# Revit family: Genie_Site_ScissorLift_GS4655a
name_source: partatom
category: Site
revit_build: Autodesk Revit 2018 (Build: 20190510_1515(x64)
units: mm (PartAtom-declared; Revit-internal decimal feet)

## family parameters
Always vertical = Yes
Cut with Voids When Loaded = No
OmniClass Number = 23.50.85.17.11
OmniClass Title = Electric and Battery Telescoping Platforms
Part Type = Normal
Round Connector Dimension = Use Diameter
Shared = No
Work Plane-Based = No

## types (1)
- GS4655
    Assembly Code = E1030900
    AssetType = Fixed
    BIMObjectName = Genie_Site_ScissorLift_GS4655
    BaseHeight = 595 mm  [stored 1.9521 ft]
    BasketHeight = 1210 mm
    C = 2640 mm
    ClassificationName = Uniclass2015
    ClassificationValue = Pr_65_80_47_95
    Color = Grey & Blue
    Cost = 0 $
    Description = The Genie® GS™-4655 scissor is a robust, eco-friendly electric scissor lift engineered for high indoor and outdoor access in restricted spaces. It offers operators an excellent combination of working height and lifting capacity capabilities with powerful electric drive motors to maximize jobsite productivity.
    DocumentationLiterature = https://www.genielift.com
    DocumentationTechnical = https://www.genielift.com
    DurationUnit = Years
    ExpectedLife = 0
    Features = Fully sealed AC electric drive motors for efficient operation indoor and outdoor and maximum runtime per battery charge. 25% gradeability with 14° breakover angle to easily get up slopes and loading ramps. Full height drive up to 16.02 m (52 ft) max. working height indoors and 10.70 m (34 ft 6 in) outdoors. Large platform workspace with 1.22 m (4 ft) slide-out extension deck. Swing out components trays for easy access. User-friendly Smart Link™ control and diagnostic system.
    Finish = Painted Steel
    IfcExportAs = IfcTransportElement
    IfcExportType = IfcTransportElementType
    Keynote = X
    Manufacturer = Genie
    ManufacturerName = Genie
    Material = Painted Steel
    Model = Genie - Scissor Lift
    ModelNumber = GS-4655
    ModelReference = Genie - Scissor Lift
    NBSDescription = Vertical lifting platforms
    NBSObjectName = Genie - Vertical lifting platforms
    NBSReference = 90-80-65/350
    NominalDepth = 1400 mm  [stored 4.59318 ft]
    NominalHeight = 2750 mm
    NominalLength = 3140 mm
    PrimaryMaterial = Steel, Paint Finish, Blue, Genie
    ProductionYear = 2019
    ReplacementCost = 0
    SecondaryMaterial = Steel, Paint Finish, Grey, Genie
    Size = 1400mm x 2750mm x 3140mm
    Type Comments = GS-4655
    TypeName = Genie - Scissor Lift
    URL = http://www.genielift.co.uk
    WarrantyDurationLabor = 0
    WarrantyDurationParts = 0
    WarrantyDurationUnit = Years
    WarrantyGuarantorLabor = http://www.genielift.co.uk
    WarrantyGuarantorParts = http://www.genielift.co.uk
    _BSBibleVersion = 15
    _BimSpecGuid = 0
    _CurrentRevision = 1
    _DistributedBy = www.bimstore.co.uk

note: [stored X ft] marks values corroborated as IEEE doubles in the binary element streams (Revit-internal decimal feet)

## geometry (parser evidence)
native form markers: Sweep x11
no freeform markers — native parametric forms only
